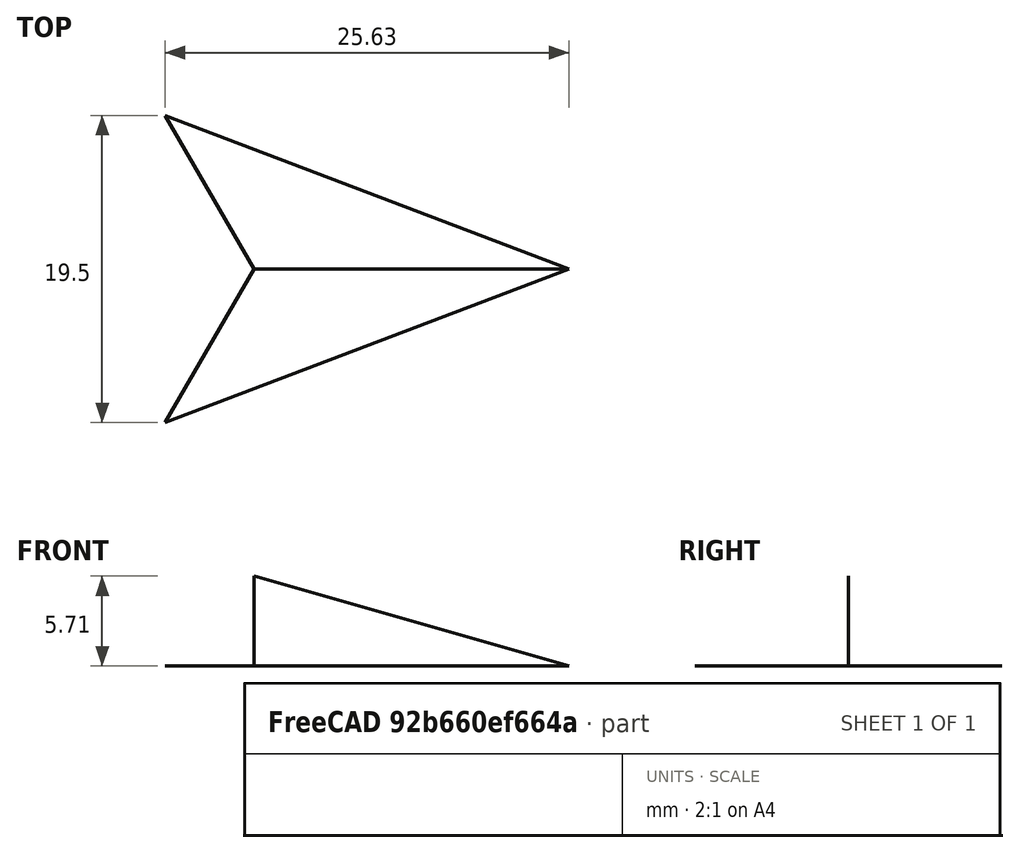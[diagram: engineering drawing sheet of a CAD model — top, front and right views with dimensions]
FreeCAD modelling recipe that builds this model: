
FCSTD DOCUMENT  (FreeCAD 0.22R37100 (Git))
Label: composit_stand3_dropper_fix_fixture
License: All rights reserved
LicenseURL: http://en.wikipedia.org/wiki/All_rights_reserved
objects: Sketcher::SketchObject×1, Part::FeaturePython×1
note: 2 computed .brp shape members not serialized (recipe doc carries the construction recipe); baked Part::Feature solids carry a one-line shape summary decoded from their .brp
EXTERNAL_REF file=composit_stand3_main.FCStd obj=Sketch

FEATURE [Sketcher::SketchObject] Sketch
  FullyConstrained = true
  Placement = pos=(0,0,0) rot=(0.57735,0.57735,0.57735;2.0944rad)
  expr: Constraints[11] = <<composit_stand3_main>>#<<main_sketch>>.Constraints.end_width - 6 mm
  sketch-geometry (5):
    g0: LineSegment StartX=-11.5 StartY=-15 StartZ=0 EndX=11.5 EndY=-15 EndZ=0
    g1: LineSegment StartX=11.5 StartY=-15 StartZ=0 EndX=11.5 EndY=0 EndZ=0
    g2: LineSegment StartX=11.5 StartY=0 StartZ=0 EndX=-11.5 EndY=0 EndZ=0
    g3: LineSegment StartX=-11.5 StartY=0 StartZ=0 EndX=-11.5 EndY=-15 EndZ=0
    g4: GeomPoint X=0 Y=-7.5 Z=0
  constraints (13):
    c: Coincident(g0,g1)
    c: Coincident(g1,g2)
    c: Coincident(g2,g3)
    c: Coincident(g3,g0)
    c: Horizontal(g0)
    c: Horizontal(g2)
    c: Vertical(g1)
    c: Vertical(g3)
    c: Symmetric(g2,g0,g4)
    c: PointOnObject(g4,g-2)
    c: PointOnObject(g1,g-1)
    c: DistanceX(g2,g2) = 23
    c: DistanceY(g1,g1) = 15
FEATURE [Part::FeaturePython] Placment  # WARN: FeaturePython — macro-defined, semantics opaque (R4)
  AttacherType = Attacher::AttachEngine3D
  ExposePlacement = true
  MarkerShape = 1
  MarkerSize = 20
  NumElements = 1
  Placement = pos=(-50,0,6) rot=(1,0,0;3.14159rad)
  Type = lattice2AttachablePlacement.AttachablePlacement
  isLattice = 1
